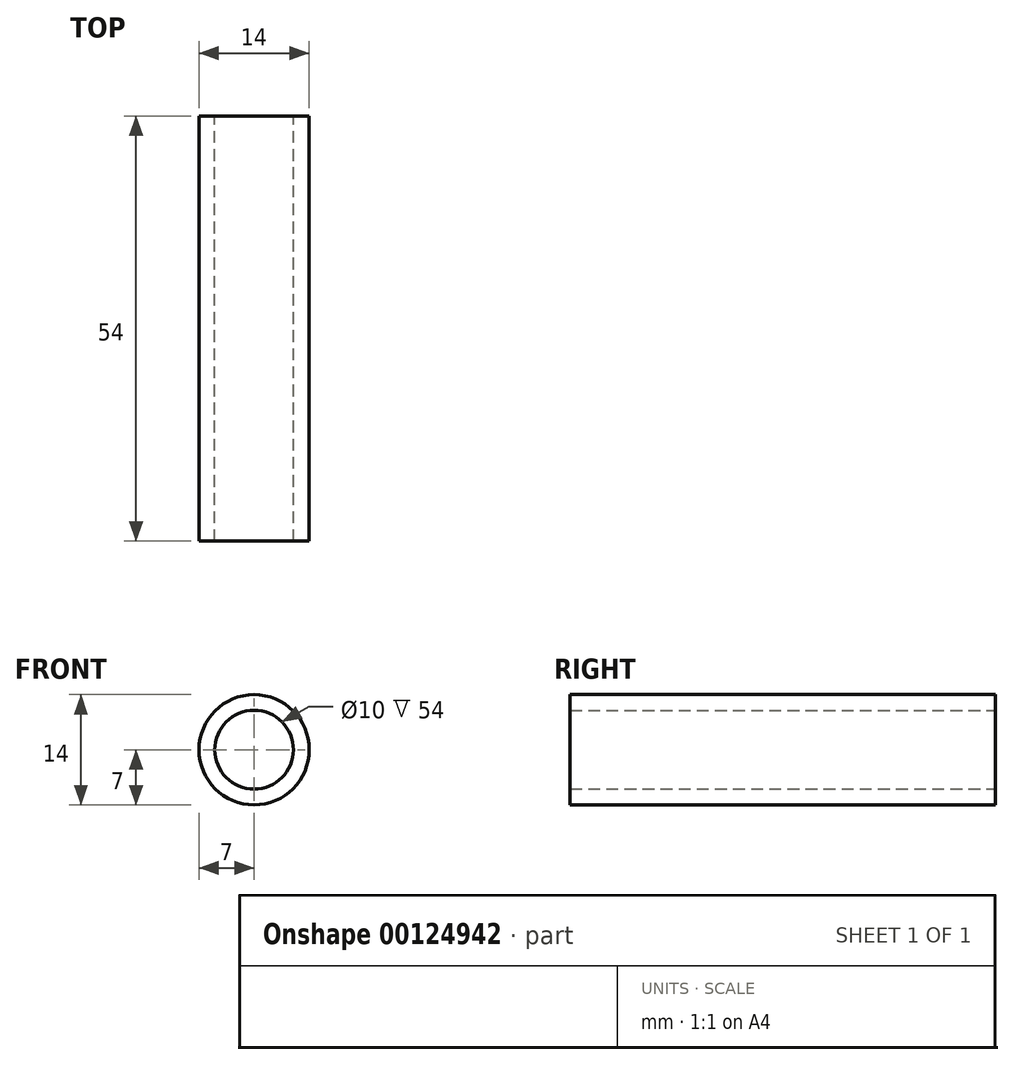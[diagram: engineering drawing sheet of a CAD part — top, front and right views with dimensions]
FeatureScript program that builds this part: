
annotation { "Feature Type Name" : "Feature", "Feature Type Description" : "" }
export const myFeature = defineFeature(function(context is Context, id is Id, definition is map)
    precondition{}
    {
        {
            var Q0;
            Q0=qCreatedBy(makeId("Front.planeOp"),FACE);
            var sketch = newSketch(context, id + "F0", { "sketchPlane" : qUnion([Q0])});
            skCircle(sketch, "E0", {"center": v(0, 0) * mm, "radius": 7 * mm});
            skCircle(sketch, "E1.0", {"center": v(0, 0) * mm, "radius": 5 * mm});
            skSolve(sketch);
        }
        {
            var Q0;
            Q0=makeQuery(id+"F0.imprint","IMPRINT",FACE,{"disambiguationData":[TD([[makeQuery(id+"F0.imprint","IMPRINT",EDGE,{"derivedFrom":sQuery(id+"F0.wireOp",EDGE,"E0")}),1.0]])]});
            extrude(context, id + "F1", {"entities" : qUnion([Q0]), "endBound" : BoundingType.SYMMETRIC, "depth" : 54 * mm});
        }
    });
